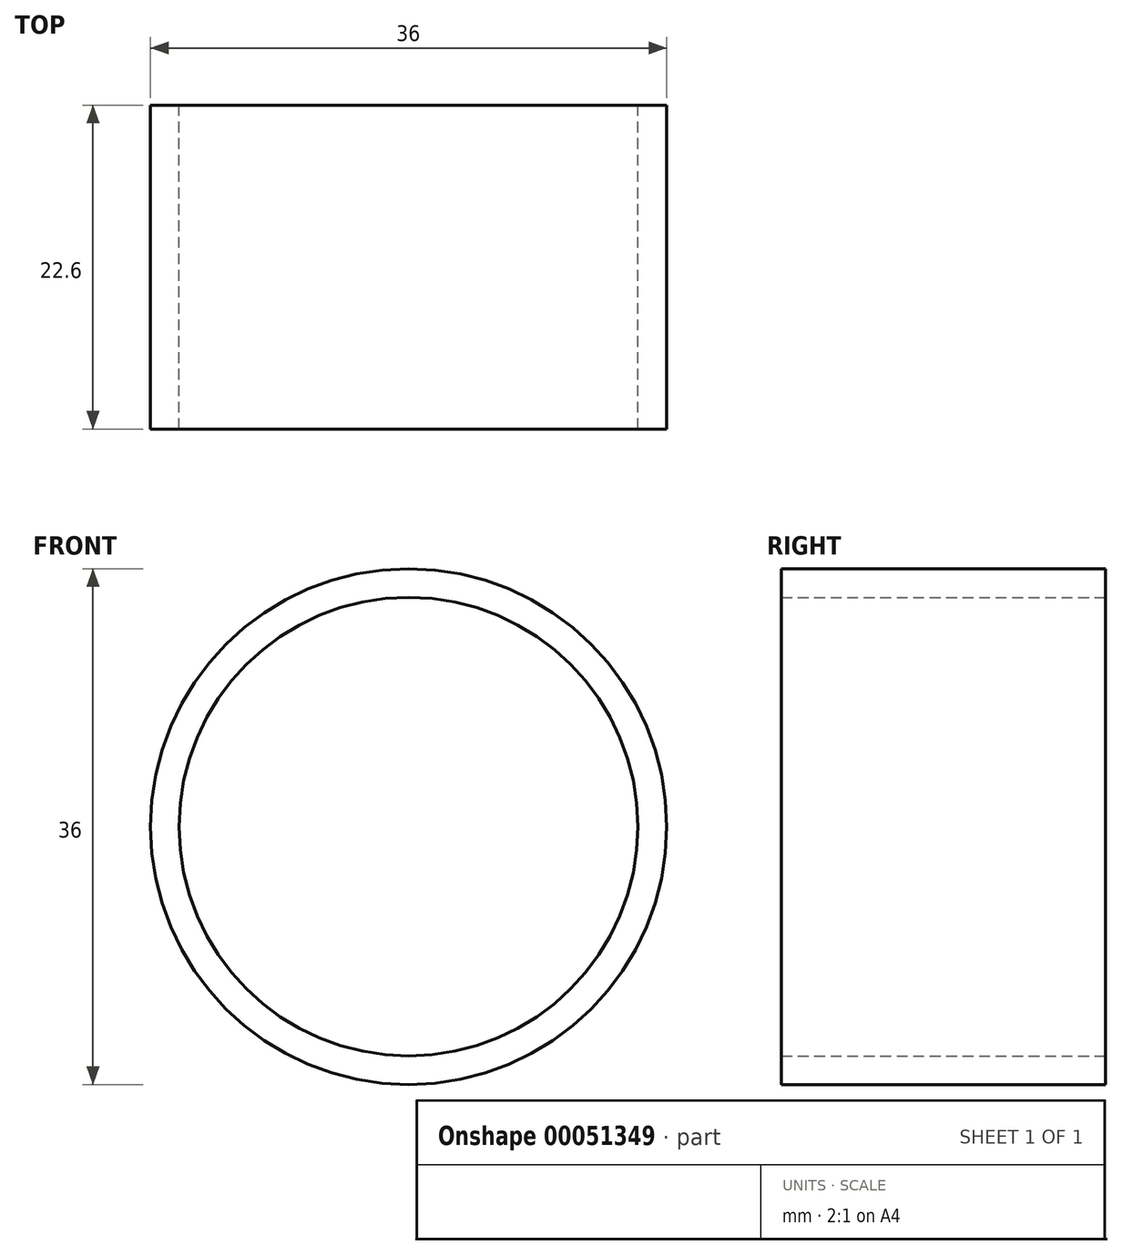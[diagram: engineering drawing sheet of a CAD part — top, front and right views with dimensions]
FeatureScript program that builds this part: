
annotation { "Feature Type Name" : "Feature", "Feature Type Description" : "" }
export const myFeature = defineFeature(function(context is Context, id is Id, definition is map)
    precondition{}
    {
        {
            var Q0;
            Q0=qCreatedBy(makeId("Front.planeOp"),FACE);
            var sketch = newSketch(context, id + "F0", { "sketchPlane" : qUnion([Q0])});
            skCircle(sketch, "E0", {"center": v(0, 0) * mm, "radius": 18 * mm});
            skCircle(sketch, "E1", {"center": v(0, 0) * mm, "radius": 16 * mm});
            skSolve(sketch);
        }
        {
            var Q0;
            Q0 = qSketchRegion(id + "F0", true);
            extrude(context, id + "F1", {"entities" : qUnion([Q0]), "depth" : (33.1 - 6 - 4.5) * mm, "symmetric" : true});
        }
    });
